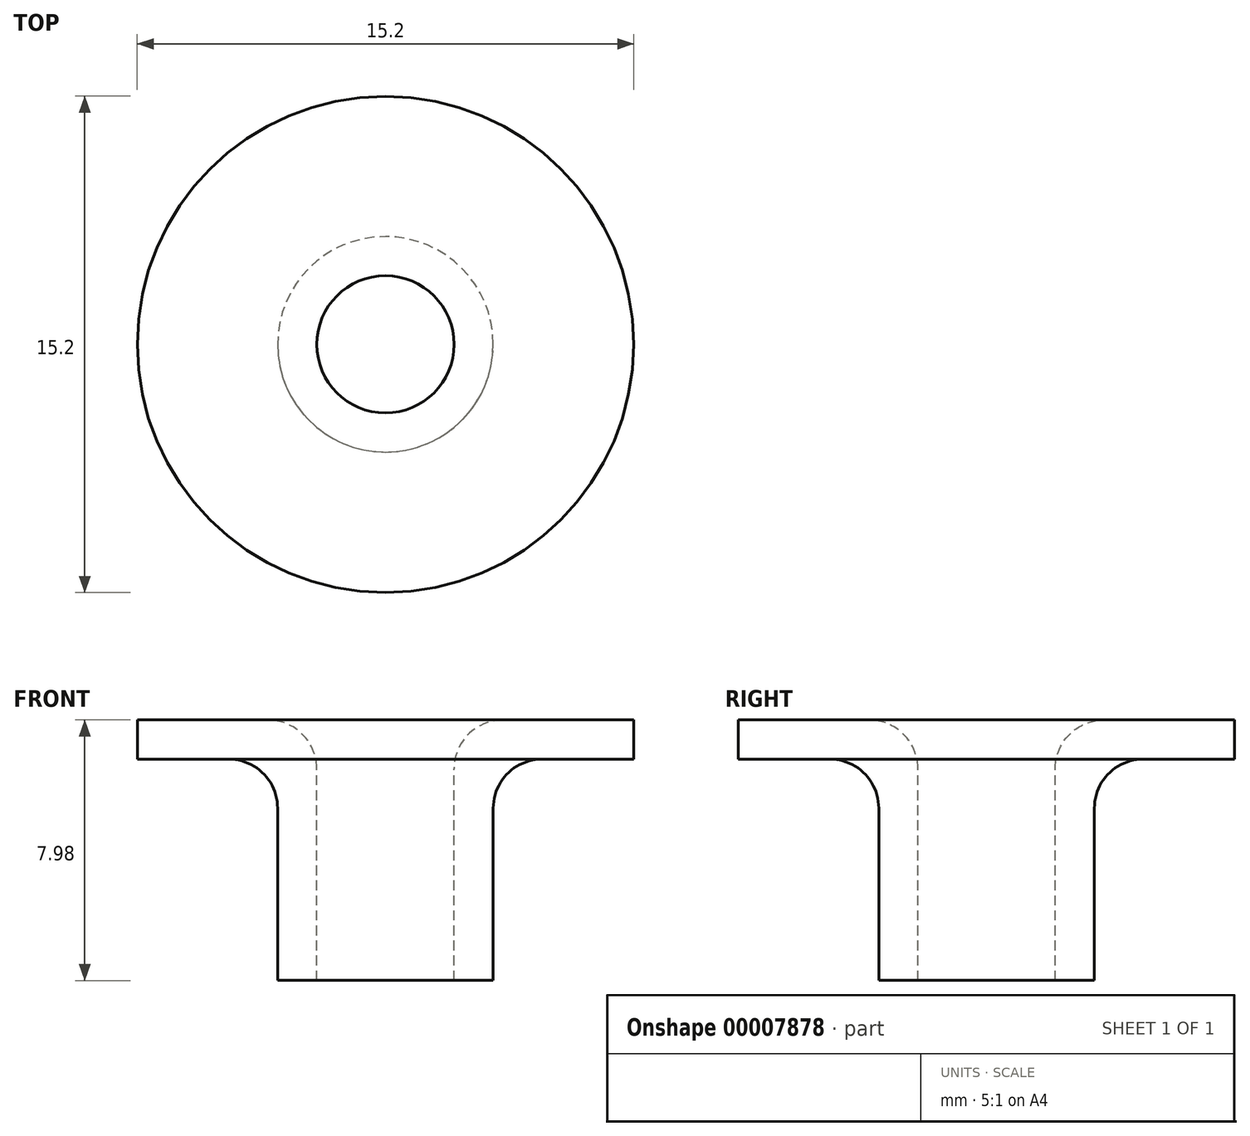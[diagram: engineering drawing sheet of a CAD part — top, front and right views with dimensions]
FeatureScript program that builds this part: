
annotation { "Feature Type Name" : "Feature", "Feature Type Description" : "" }
export const myFeature = defineFeature(function(context is Context, id is Id, definition is map)
    precondition{}
    {
        {
            var Q0;
            Q0=qCreatedBy(makeId("Front.planeOp"),FACE);
            var sketch = newSketch(context, id + "F0", { "sketchPlane" : qUnion([Q0])});
            skLineSegment(sketch, "E0", {"start": v(0, 69.18) * mm, "end": v(0, -69.18) * mm, "construction": true});
            skLineSegment(sketch, "E1", {"start": v(7.6, 1.2) * mm, "end": v(7.6, 0) * mm});
            skLineSegment(sketch, "E2", {"start": v(7.6, 0) * mm, "end": v(3.3, 0) * mm});
            skLineSegment(sketch, "E3", {"start": v(3.3, 0) * mm, "end": v(3.3, -6.78) * mm});
            skLineSegment(sketch, "E4", {"start": v(3.3, -6.78) * mm, "end": v(2.1, -6.78) * mm});
            skLineSegment(sketch, "E5", {"start": v(2.1, -6.78) * mm, "end": v(2.1, 1.2) * mm});
            skLineSegment(sketch, "E6", {"start": v(2.1, 1.2) * mm, "end": v(7.6, 1.2) * mm});
            skLineSegment(sketch, "E7", {"start": v(2.5, 1.2) * mm, "end": v(2.5, -6.78) * mm, "construction": true});
            skSolve(sketch);
        }
        {
            var Q0;
            Q0=makeQuery(id+"F0.imprint","IMPRINT",FACE,{"disambiguationData":[TD([[makeQuery(id+"F0.imprint","IMPRINT",EDGE,{"derivedFrom":sQuery(id+"F0.wireOp",EDGE,"E1")}),-1.0]])]});
            var Q1;
            Q1=sQuery(id+"F0.wireOp",EDGE,"E0");
            revolve(context, id + "F1", {"entities" : qUnion([Q0]), "axis" : qUnion([Q1]), "revolveType" : RevolveType.FULL});
        }
        {
            var Q0;
            Q0=makeQuery(id+"F1.opRevolve","SWEPT_EDGE",EDGE,{"disambiguationData":[OSD([sQuery(id+"F0.wireOp",EDGE,"E5"),sQuery(id+"F0.wireOp",EDGE,"E6")])]});
            var Q1;
            Q1=makeQuery(id+"F1.opRevolve","SWEPT_EDGE",EDGE,{"disambiguationData":[OSD([sQuery(id+"F0.wireOp",EDGE,"E2"),sQuery(id+"F0.wireOp",EDGE,"E3")])]});
            fillet(context, id + "F2", {"entities" : qUnion([Q0, Q1]), "radius" : 1.5 * mm, "tangentPropagation" : true, "allowEdgeOverflow" : false});
        }
    });
